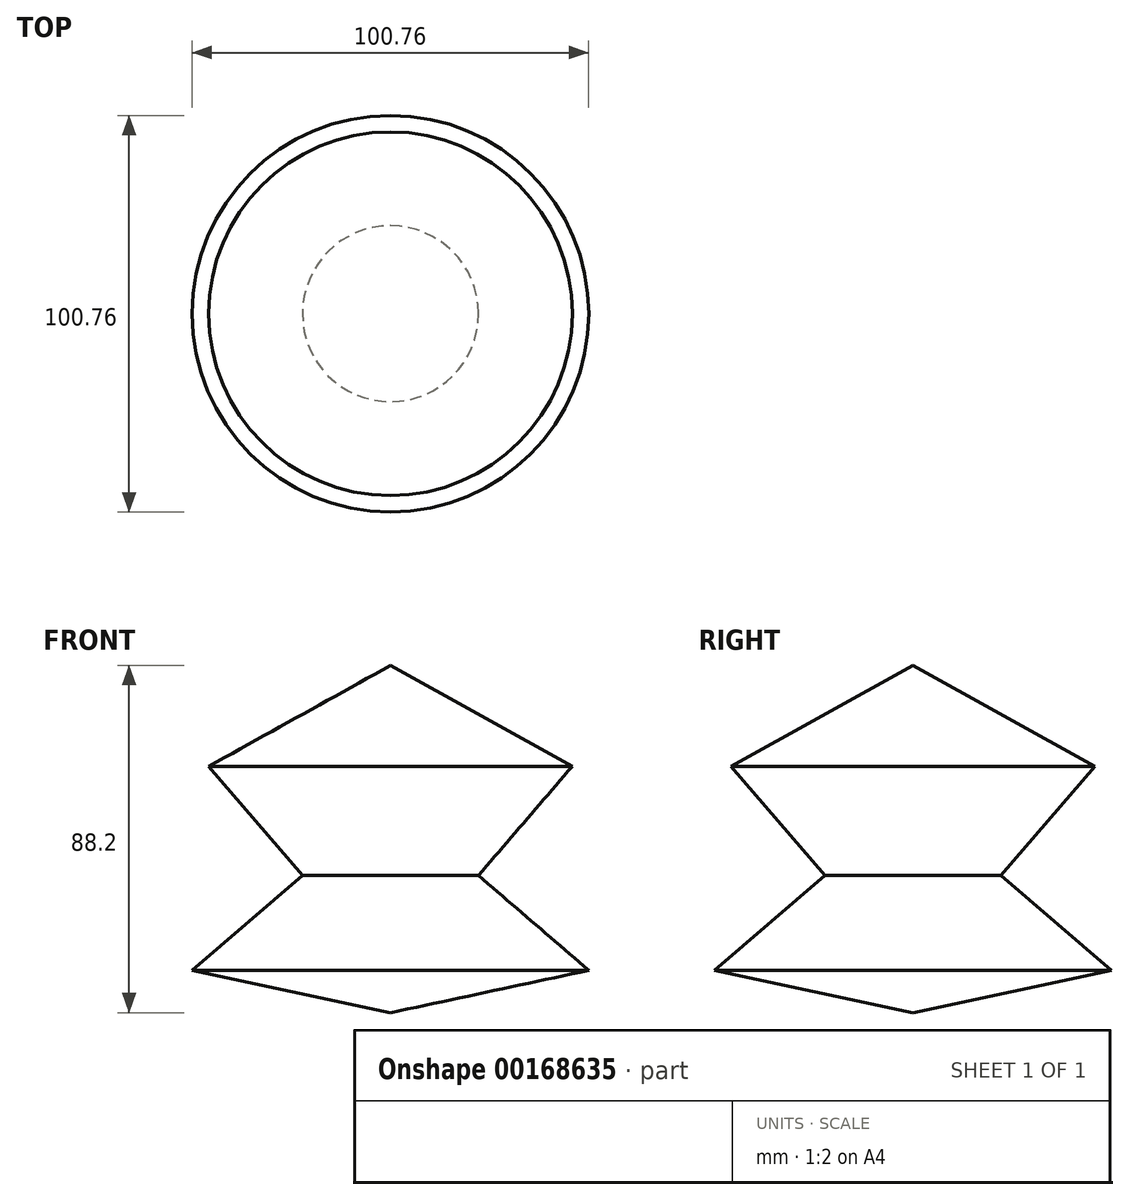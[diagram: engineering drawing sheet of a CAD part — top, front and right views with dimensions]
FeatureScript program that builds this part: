
annotation { "Feature Type Name" : "Feature", "Feature Type Description" : "" }
export const myFeature = defineFeature(function(context is Context, id is Id, definition is map)
    precondition{}
    {
        {
            var Q0;
            Q0=qCreatedBy(makeId("Front.planeOp"),FACE);
            var sketch = newSketch(context, id + "F0", { "sketchPlane" : qUnion([Q0])});
            skLineSegment(sketch, "E0", {"start": v(-43.36, 56.17) * mm, "end": v(-43.36, -32.03) * mm});
            skLineSegment(sketch, "E1", {"start": v(-43.36, 56.17) * mm, "end": v(2.83, 30.54) * mm});
            skLineSegment(sketch, "E2", {"start": v(2.83, 30.54) * mm, "end": v(-21, 2.83) * mm});
            skLineSegment(sketch, "E3", {"start": v(-21, 2.83) * mm, "end": v(7.02, -21.28) * mm});
            skLineSegment(sketch, "E4", {"start": v(7.02, -21.28) * mm, "end": v(-43.36, -32.03) * mm});
            skSolve(sketch);
        }
        {
            var Q0;
            Q0=makeQuery(id+"F0.imprint","IMPRINT",FACE,{"disambiguationData":[TD([[makeQuery(id+"F0.imprint","IMPRINT",EDGE,{"derivedFrom":sQuery(id+"F0.wireOp",EDGE,"E0")}),1.0]])]});
            var Q1;
            Q1=sQuery(id+"F0.wireOp",EDGE,"E0");
            revolve(context, id + "F1", {"entities" : qUnion([Q0]), "axis" : qUnion([Q1]), "revolveType" : RevolveType.FULL});
        }
    });
